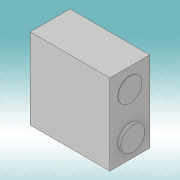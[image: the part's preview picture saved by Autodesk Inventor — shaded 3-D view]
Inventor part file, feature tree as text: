
AUTODESK INVENTOR PART (.ipt)
format: ipt  version: 2019 (Build 230136000, 136)  size: 118,784 bytes
history: native  units: mm
features: extrude x5, sketch x3
ambient origin geometry x8: Origin, YZ Plane, XZ Plane, XY Plane, X Axis, Y Axis, Z Axis, Center Point
bodies: Solid1 (feature_tree)
feature tree (8):
  extrude  "Extrusion1"  Depth=40.5mm
  sketch  "Sketch2"  dims[d2=20.0mm d3=0.0mm d4=12.0mm]
  extrude  "Extrusion2"  Depth=20.0mm
  sketch  "Sketch3"  dims[d5=10.0mm d6=10.0mm d7=1.5mm d8=0.0mm d11=1.5mm d12=0.0mm d13=0.1mm d14=0.0mm d15=0.1mm d16=0.0mm]
  extrude  "Extrusion4"  Depth=10.0mm
  extrude  "Extrusion5"  Depth=1.5mm TaperAngle=0.0deg
  extrude  "Extrusion6"  Depth=1.5mm TaperAngle=0.0deg
  sketch  "Sketch1"  dims[d0=40.0mm d1=40.5mm]
